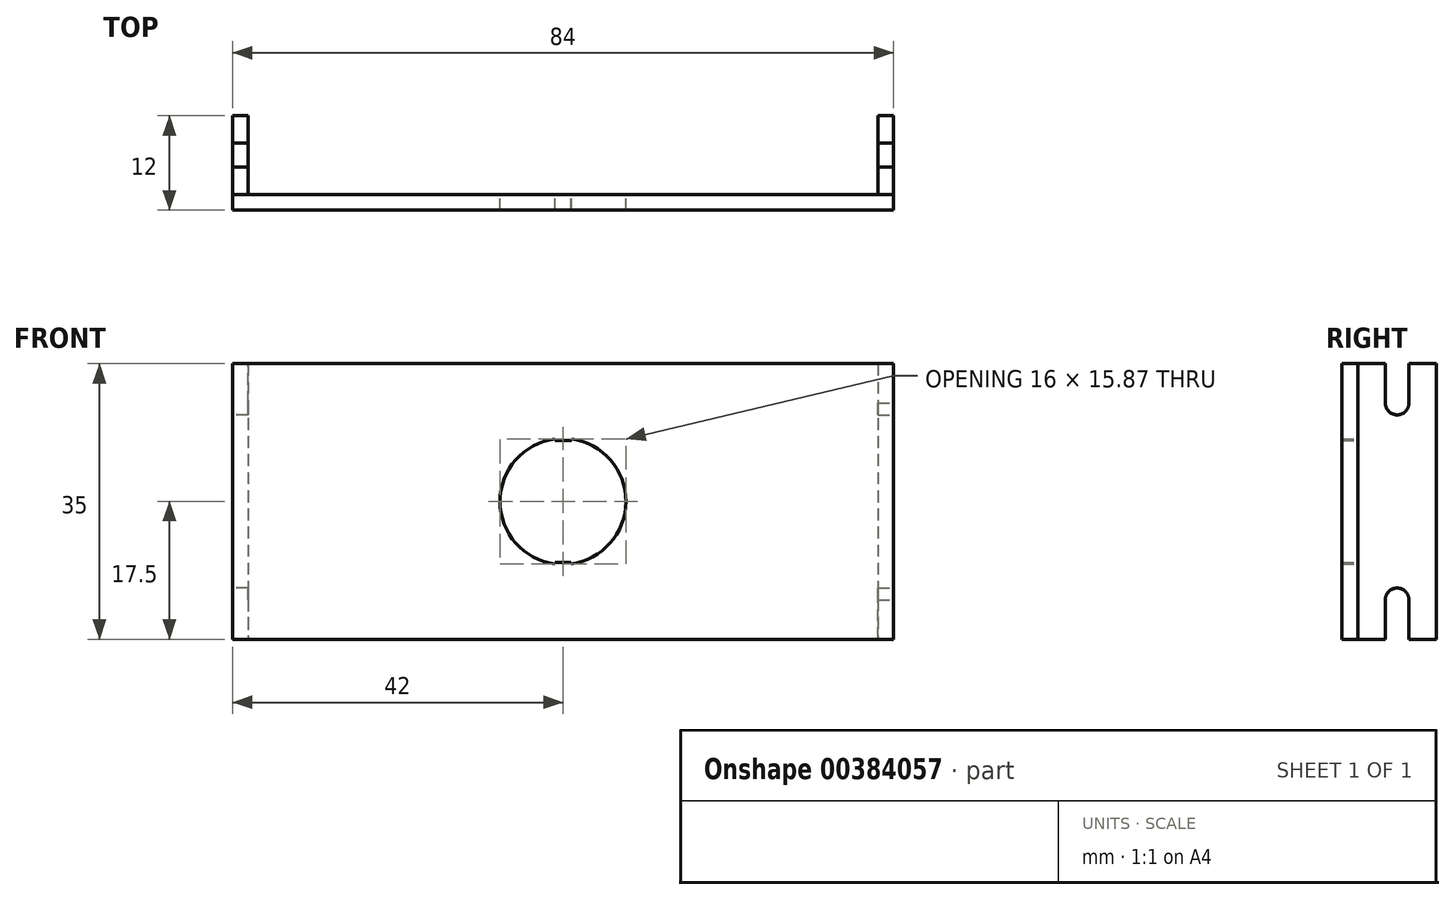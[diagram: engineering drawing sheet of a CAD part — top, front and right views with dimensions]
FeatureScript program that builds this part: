
annotation { "Feature Type Name" : "Feature", "Feature Type Description" : "" }
export const myFeature = defineFeature(function(context is Context, id is Id, definition is map)
    precondition{}
    {
        {
            var Q0;
            Q0=qCreatedBy(makeId("Front.planeOp"),FACE);
            var sketch = newSketch(context, id + "F0", { "sketchPlane" : qUnion([Q0])});
            skLineSegment(sketch, "E0.bottom", {"start": v(-42, 17.5) * mm, "end": v(42, 17.5) * mm});
            skLineSegment(sketch, "E0.top", {"start": v(-42, -17.5) * mm, "end": v(42, -17.5) * mm});
            skLineSegment(sketch, "E0.left", {"start": v(-42, 17.5) * mm, "end": v(-42, -17.5) * mm});
            skLineSegment(sketch, "E0.right", {"start": v(42, 17.5) * mm, "end": v(42, -17.5) * mm});
            skArc(sketch, "E1", {"start": v(-1, 7.94) * mm, "mid": v(-8, 0) * mm, "end": v(-1, -7.94) * mm});
            skLineSegment(sketch, "E2.top", {"start": v(-1, 7.74) * mm, "end": v(1.07, 7.74) * mm});
            skLineSegment(sketch, "E2.left", {"start": v(-1, 7.94) * mm, "end": v(-1, 7.74) * mm});
            skLineSegment(sketch, "E2.right", {"start": v(1.07, 7.93) * mm, "end": v(1.07, 7.74) * mm});
            skLineSegment(sketch, "E3.top", {"start": v(-1, -7.74) * mm, "end": v(1, -7.74) * mm});
            skLineSegment(sketch, "E3.left", {"start": v(-1, -7.94) * mm, "end": v(-1, -7.74) * mm});
            skLineSegment(sketch, "E3.right", {"start": v(1, -7.94) * mm, "end": v(1, -7.74) * mm});
            skArc(sketch, "E4.trimOffspring", {"start": v(1, -7.94) * mm, "mid": v(8, -0.03) * mm, "end": v(1.07, 7.93) * mm});
            skSolve(sketch);
        }
        {
            var Q0;
            Q0 = qSketchRegion(id + "F0", true);
            extrude(context, id + "F1", {"entities" : qUnion([Q0]), "depth" : 2 * mm});
        }
        {
            var Q0;
            Q0=makeQuery(id+"F1.opExtrude","SWEPT_FACE",FACE,{"disambiguationData":[OSD([sQuery(id+"F0.wireOp",EDGE,"E0.right")])]});
            var sketch = newSketch(context, id + "F2", { "sketchPlane" : qUnion([Q0])});
            skLineSegment(sketch, "E5.bottom", {"start": v(0, 17.5) * mm, "end": v(3.5, 17.5) * mm});
            skLineSegment(sketch, "E5.top", {"start": v(0, -17.5) * mm, "end": v(3.5, -17.5) * mm});
            skLineSegment(sketch, "E5.left", {"start": v(0, 17.5) * mm, "end": v(0, -17.5) * mm});
            skLineSegment(sketch, "E5.right", {"start": v(10, 17.5) * mm, "end": v(10, -17.5) * mm});
            skArc(sketch, "E6", {"start": v(3.5, 12.52) * mm, "mid": v(4.99, 11) * mm, "end": v(6.5, 12.5) * mm});
            skArc(sketch, "E7", {"start": v(6.5, -12.5) * mm, "mid": v(4.99, -11) * mm, "end": v(3.5, -12.52) * mm});
            skLineSegment(sketch, "E8", {"start": v(3.5, 17.5) * mm, "end": v(3.5, 12.52) * mm});
            skLineSegment(sketch, "E9", {"start": v(6.5, 17.5) * mm, "end": v(6.5, 12.5) * mm});
            skLineSegment(sketch, "E10.trimOffspring", {"start": v(6.5, 17.5) * mm, "end": v(10, 17.5) * mm});
            skLineSegment(sketch, "E11.MirrorCS", {"start": v(3.5, -17.5) * mm, "end": v(3.5, -12.52) * mm});
            skArc(sketch, "E12.MirrorCS", {"start": v(3.5, -12.52) * mm, "mid": v(4.99, -11) * mm, "end": v(6.5, -12.5) * mm});
            skLineSegment(sketch, "E13.MirrorCS", {"start": v(6.5, -17.5) * mm, "end": v(6.5, -12.5) * mm});
            skLineSegment(sketch, "E14.trimOffspring", {"start": v(6.5, -17.5) * mm, "end": v(10, -17.5) * mm});
            skSolve(sketch);
        }
        {
            var Q0;
            Q0 = qSketchRegion(id + "F2", true);
            extrude(context, id + "F3", {"entities" : qUnion([Q0]), "oppositeDirection" : true, "depth" : 2 * mm});
        }
        {
            var Q0;
            Q0=makeQuery(id+"F1.opExtrude","SWEPT_FACE",FACE,{"disambiguationData":[OSD([sQuery(id+"F0.wireOp",EDGE,"E0.left")])]});
            var sketch = newSketch(context, id + "F4", { "sketchPlane" : qUnion([Q0])});
            skLineSegment(sketch, "E15.bottom", {"start": v(-10, 17.5) * mm, "end": v(-6.5, 17.5) * mm});
            skLineSegment(sketch, "E15.top", {"start": v(-10, -17.5) * mm, "end": v(-6.5, -17.5) * mm});
            skLineSegment(sketch, "E15.left", {"start": v(-10, 17.5) * mm, "end": v(-10, -17.5) * mm});
            skLineSegment(sketch, "E15.right", {"start": v(0, 17.5) * mm, "end": v(0, -17.5) * mm});
            skArc(sketch, "E16", {"start": v(-6.5, 12.5) * mm, "mid": v(-5, 11) * mm, "end": v(-3.5, 12.5) * mm});
            skArc(sketch, "E17", {"start": v(-3.5, -12.5) * mm, "mid": v(-5, -11) * mm, "end": v(-6.5, -12.5) * mm});
            skLineSegment(sketch, "E18", {"start": v(-6.5, 12.5) * mm, "end": v(-6.5, 17.5) * mm});
            skLineSegment(sketch, "E19", {"start": v(-3.5, 12.5) * mm, "end": v(-3.5, 17.5) * mm});
            skLineSegment(sketch, "E20.trimOffspring", {"start": v(-3.5, 17.5) * mm, "end": v(0, 17.5) * mm});
            skLineSegment(sketch, "E21.MirrorCS", {"start": v(-3.5, -12.5) * mm, "end": v(-3.5, -17.5) * mm});
            skLineSegment(sketch, "E22.MirrorCS", {"start": v(-6.5, -12.5) * mm, "end": v(-6.5, -17.5) * mm});
            skLineSegment(sketch, "E23.trimOffspring", {"start": v(-3.5, -17.5) * mm, "end": v(0, -17.5) * mm});
            skSolve(sketch);
        }
        {
            var Q0;
            Q0=makeQuery(id+"F4.imprint","IMPRINT",FACE,{"disambiguationData":[TD([[makeQuery(id+"F4.imprint","IMPRINT",EDGE,{"derivedFrom":sQuery(id+"F4.wireOp",EDGE,"E15.bottom")}),-1.0]])]});
            extrude(context, id + "F5", {"entities" : qUnion([Q0]), "oppositeDirection" : true, "depth" : 2 * mm});
        }
    });
